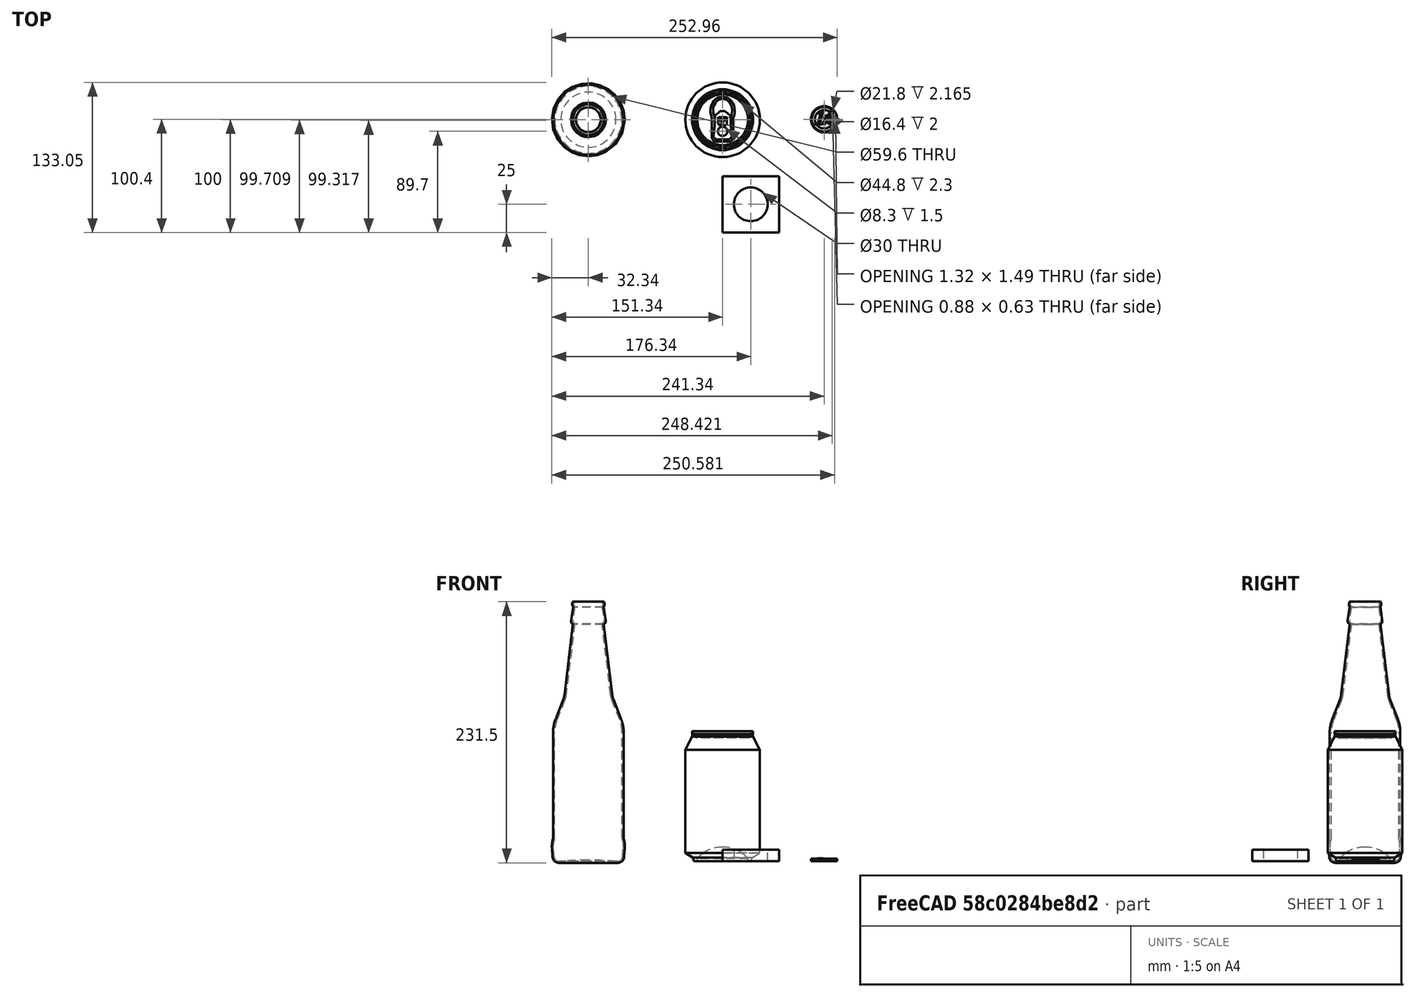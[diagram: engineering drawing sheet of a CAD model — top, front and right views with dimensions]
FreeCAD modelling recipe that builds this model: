
FCSTD DOCUMENT  (FreeCAD 1.0R38806 (Git))
Label: 03-bottle-can-euro_CON_DIFERENCIA_EJEMPLO.fcstd
License: All rights reserved
LicenseURL: http://en.wikipedia.org/wiki/All_rights_reserved
objects: Part::Feature×3, Part::Cut×2, Part::Box×1, Part::Cylinder×1
note: 7 computed .brp shape members not serialized (recipe doc carries the construction recipe); baked Part::Feature solids carry a one-line shape summary decoded from their .brp

FEATURE [Part::Feature] Compound001  label="Euro-coin"
  Placement = pos=(90,100,0) rot=(0,0,1;0rad)
  shape: bbox 23.25 x 23.25 x 2.414 mm, 903 faces, 22 solids (baked)
FEATURE [Part::Feature] Thickness001  label="Bottle"
  Placement = pos=(-119,100,0) rot=(0,0,1;0rad)
  shape: bbox 71.75 x 74.3 x 235 mm, 40 faces (baked)
FEATURE [Part::Feature] Fusion001  label="Can"
  Placement = pos=(0,100,0) rot=(0,0,1;0rad)
  shape: bbox 66.1 x 66.1 x 115.2 mm, 53 faces (baked)
FEATURE [Part::Box] Box  label="Cube"
  AttacherType = Attacher::AttachEngine3D
  Height = 10
  Length = 50
  Width = 50
FEATURE [Part::Cylinder] Cylinder
  Angle = 360
  AttacherType = Attacher::AttachEngine3D
  FirstAngle = 0
  Height = 40
  Placement = pos=(25,25,-12) rot=(0,0,1;0rad)
  Radius = 15
  SecondAngle = 0
FEATURE [Part::Cut] Cut
  Base = -> Box
  Refine = true
  Tool = -> Cylinder
FEATURE [Part::Cut] Cut001
  Base = -> Box
  Refine = true
  Tool = -> Cylinder
